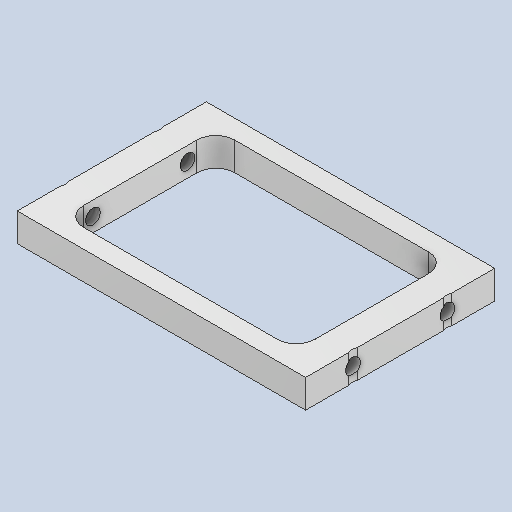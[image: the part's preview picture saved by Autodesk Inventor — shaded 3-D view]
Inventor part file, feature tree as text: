
AUTODESK INVENTOR PART (.ipt)
format: ipt  version: 2025.1 (Build 291241000, 241)  size: 206,336 bytes
history: native  units: mm
features: sketch x2, other x1, extrude x1, fillet x1, hole x1
ambient origin geometry x8: Origin, YZ Plane, XZ Plane, XY Plane, X Axis, Y Axis, Z Axis, Center Point
bodies: Body1 (feature_tree)
feature tree (6):
  other  "ソリッド1"
  extrude  "押し出し1"  Depth=30.5mm
  fillet  "フィレット1"  Radius=20.0mm
  hole  "穴1"  [1 undecoded]
  sketch  "スケッチ1"
  sketch  "スケッチ2"
note: 1 required parameter value undecoded (feature->parameter linkage not recoverable at this tier; creation-order binding heuristic only, values carry confidence <= 0.55)
